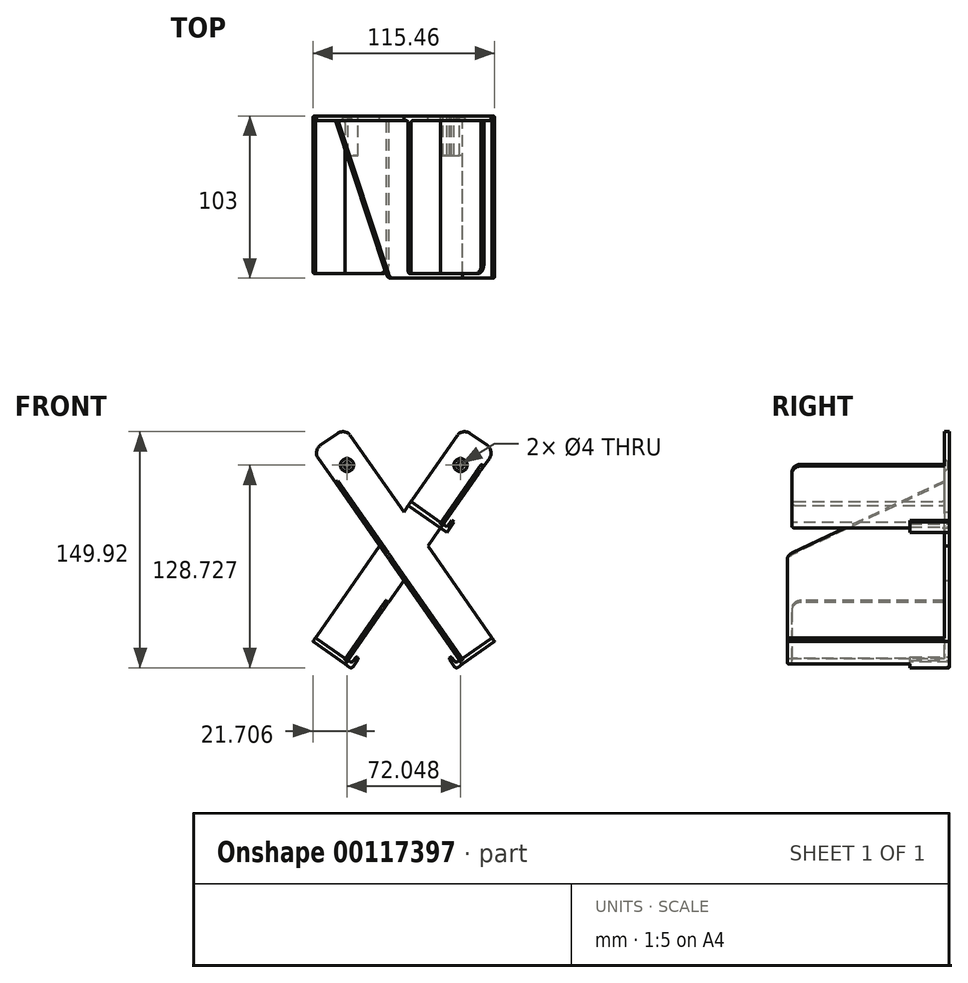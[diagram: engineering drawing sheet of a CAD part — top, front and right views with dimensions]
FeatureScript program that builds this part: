
annotation { "Feature Type Name" : "Feature", "Feature Type Description" : "" }
export const myFeature = defineFeature(function(context is Context, id is Id, definition is map)
    precondition{}
    {
        {
            var Q0;
            Q0=qCreatedBy(makeId("Front.planeOp"),FACE);
            var sketch = newSketch(context, id + "F0", { "sketchPlane" : qUnion([Q0])});
            skLineSegment(sketch, "E0", {"start": v(-100, 75) * mm, "end": v(-100, -75) * mm, "construction": true});
            skPoint(sketch, "E1", {"position": v(-100, 0) * mm});
            skLineSegment(sketch, "E2", {"start": v(57.73, 60.66) * mm, "end": v(-37.26, -75) * mm});
            skLineSegment(sketch, "E3", {"start": v(-37.26, -75) * mm, "end": v(-57.73, -60.66) * mm});
            skLineSegment(sketch, "E4", {"start": v(-57.73, -60.66) * mm, "end": v(37.26, 75) * mm});
            skLineSegment(sketch, "E5", {"start": v(37.26, 75) * mm, "end": v(57.73, 60.66) * mm});
            skLineSegment(sketch, "E6", {"start": v(47.5, 67.83) * mm, "end": v(-47.5, -67.83) * mm, "construction": true});
            skLineSegment(sketch, "E7", {"start": v(-10.24, 7.17) * mm, "end": v(10.24, -7.17) * mm, "construction": true});
            skPoint(sketch, "E8", {"position": v(0, 0) * mm});
            skLineSegment(sketch, "E9", {"start": v(-37.26, 75) * mm, "end": v(57.73, -60.66) * mm});
            skLineSegment(sketch, "E10", {"start": v(57.73, -60.66) * mm, "end": v(37.26, -75) * mm});
            skLineSegment(sketch, "E11", {"start": v(37.26, -75) * mm, "end": v(-57.73, 60.66) * mm});
            skLineSegment(sketch, "E12", {"start": v(-57.73, 60.66) * mm, "end": v(-37.26, 75) * mm});
            skLineSegment(sketch, "E13", {"start": v(-47.5, 67.83) * mm, "end": v(47.5, -67.83) * mm, "construction": true});
            skLineSegment(sketch, "E14", {"start": v(-10.24, -7.17) * mm, "end": v(10.24, 7.17) * mm, "construction": true});
            skLineSegment(sketch, "E15", {"start": v(37.26, -75) * mm, "end": v(33.16, -77.87) * mm});
            skLineSegment(sketch, "E16", {"start": v(33.16, -77.87) * mm, "end": v(28.57, -71.31) * mm});
            skLineSegment(sketch, "E17", {"start": v(28.57, -71.31) * mm, "end": v(30.2, -70.17) * mm});
            skLineSegment(sketch, "E18", {"start": v(30.2, -70.17) * mm, "end": v(33.08, -74.26) * mm});
            skLineSegment(sketch, "E19", {"start": v(33.08, -74.26) * mm, "end": v(35.54, -72.54) * mm});
            skLineSegment(sketch, "E20", {"start": v(-37.26, -75) * mm, "end": v(-33.16, -77.87) * mm});
            skLineSegment(sketch, "E21", {"start": v(-33.16, -77.87) * mm, "end": v(-28.57, -71.31) * mm});
            skLineSegment(sketch, "E22", {"start": v(-28.57, -71.31) * mm, "end": v(-30.2, -70.17) * mm});
            skLineSegment(sketch, "E23", {"start": v(-30.2, -70.17) * mm, "end": v(-33.08, -74.26) * mm});
            skLineSegment(sketch, "E24", {"start": v(-33.08, -74.26) * mm, "end": v(-35.54, -72.54) * mm});
            skLineSegment(sketch, "E25", {"start": v(23.32, 11.51) * mm, "end": v(27.42, 8.64) * mm});
            skLineSegment(sketch, "E26", {"start": v(27.42, 8.64) * mm, "end": v(32, 15.2) * mm});
            skLineSegment(sketch, "E27", {"start": v(32, 15.2) * mm, "end": v(30.37, 16.34) * mm});
            skLineSegment(sketch, "E28", {"start": v(30.37, 16.34) * mm, "end": v(27.5, 12.25) * mm});
            skLineSegment(sketch, "E29", {"start": v(27.5, 12.25) * mm, "end": v(25.04, 13.97) * mm});
            skLineSegment(sketch, "E30", {"start": v(-35.54, -72.54) * mm, "end": v(-56.01, -58.2) * mm});
            skLineSegment(sketch, "E31", {"start": v(25.04, 13.97) * mm, "end": v(4.56, 28.3) * mm});
            skLineSegment(sketch, "E32", {"start": v(23.32, 11.51) * mm, "end": v(2.84, 25.85) * mm});
            skCircle(sketch, "E33", {"center": v(36.02, 51.45) * mm, "radius": 2 * mm});
            skCircle(sketch, "E34", {"center": v(-36.02, 51.45) * mm, "radius": 2 * mm});
            skSolve(sketch);
        }
        {
            var Q0;
            {var subQ0=sQuery(id+"F0.wireOp",EDGE,"E12");Q0=makeQuery(id+"F0.imprint","IMPRINT",FACE,{"disambiguationData":[TD([[makeQuery(id+"F0.imprint","IMPRINT",EDGE,{"derivedFrom":subQ0}),-1.0]])]});}
            var Q1;
            {var subQ3=sQuery(id+"F0.wireOp",EDGE,"E2");var subQ5=sQuery(id+"F0.wireOp",EDGE,"E9");var subQ7=makeQuery(id+"F0.imprint","INTERSECT",VERTEX,{"derivedFrom":[subQ3,subQ5]});Q1=makeQuery(id+"F0.imprint","IMPRINT",FACE,{"disambiguationData":[TD([[makeQuery(id+"F0.imprint","IMPRINT",EDGE,{"disambiguationData":[TD([[subQ7,-1.0]])],"derivedFrom":subQ3}),-1.0]])]});}
            var Q2;
            {var subQ0=sQuery(id+"F0.wireOp",EDGE,"E5");Q2=makeQuery(id+"F0.imprint","IMPRINT",FACE,{"disambiguationData":[TD([[makeQuery(id+"F0.imprint","IMPRINT",EDGE,{"derivedFrom":subQ0}),-1.0]])]});}
            var Q3;
            {var subQ5=sQuery(id+"F0.wireOp",EDGE,"E32");Q3=makeQuery(id+"F0.imprint","IMPRINT",FACE,{"disambiguationData":[TD([[makeQuery(id+"F0.imprint","IMPRINT",EDGE,{"derivedFrom":subQ5}),1.0]])]});}
            var Q4;
            {var subQ2=sQuery(id+"F0.wireOp",EDGE,"E31");Q4=makeQuery(id+"F0.imprint","IMPRINT",FACE,{"disambiguationData":[TD([[makeQuery(id+"F0.imprint","IMPRINT",EDGE,{"derivedFrom":subQ2}),1.0]])]});}
            var Q5;
            {var subQ0=sQuery(id+"F0.wireOp",EDGE,"E30");Q5=makeQuery(id+"F0.imprint","IMPRINT",FACE,{"disambiguationData":[TD([[makeQuery(id+"F0.imprint","IMPRINT",EDGE,{"derivedFrom":subQ0}),-1.0]])]});}
            var Q6;
            {var subQ6=sQuery(id+"F0.wireOp",EDGE,"E10");Q6=makeQuery(id+"F0.imprint","IMPRINT",FACE,{"disambiguationData":[TD([[makeQuery(id+"F0.imprint","IMPRINT",EDGE,{"derivedFrom":subQ6}),-1.0]])]});}
            var Q7;
            {var subQ2=sQuery(id+"F0.wireOp",EDGE,"E3");Q7=makeQuery(id+"F0.imprint","IMPRINT",FACE,{"disambiguationData":[TD([[makeQuery(id+"F0.imprint","IMPRINT",EDGE,{"derivedFrom":subQ2}),-1.0]])]});}
            extrude(context, id + "F1", {"entities" : qUnion([Q0, Q1, Q2, Q3, Q4, Q5, Q6, Q7]), "depth" : 3 * mm});
        }
        {
            var Q0;
            {var subQ0=sQuery(id+"F0.wireOp",EDGE,"E11");Q0=makeQuery(id+"F1.opExtrude","SWEPT_FACE",FACE,{"disambiguationData":[OSD([subQ0]),TDD([makeQuery(id+"F0.imprint","IMPRINT",EDGE,{"disambiguationData":[TD([[makeQuery(id+"F0.imprint","INTERSECT",VERTEX,{"derivedFrom":[sQuery(id+"F0.wireOp",EDGE,"E10"),subQ0]}),-1.0]])],"derivedFrom":subQ0})])]});}
            cPlane(context, id + "F2", {"entities" : qUnion([Q0]), "cplaneType" : CPlaneType.OFFSET, "offset" : 0 * mm, "width" : 150 * mm, "height" : 150 * mm});
        }
        {
            var Q0;
            Q0=qCreatedBy(id+"F2.planeOp",FACE);
            var sketch = newSketch(context, id + "F3", { "sketchPlane" : qUnion([Q0])});
            skLineSegment(sketch, "E35.bottom", {"start": v(103, -82.8) * mm, "end": v(3, -82.8) * mm});
            skLineSegment(sketch, "E35.top", {"start": v(103, 0.2) * mm, "end": v(3, 0.2) * mm});
            skLineSegment(sketch, "E35.left", {"start": v(103, -82.8) * mm, "end": v(103, 0.2) * mm});
            skLineSegment(sketch, "E35.right", {"start": v(3, -82.8) * mm, "end": v(3, 0.2) * mm});
            skLineSegment(sketch, "E36", {"start": v(3, 0.2) * mm, "end": v(3, 57.93) * mm});
            skLineSegment(sketch, "E37", {"start": v(3, 57.93) * mm, "end": v(103, 0.2) * mm});
            skCircle(sketch, "E38.cCircle", {"center": v(48.07, -28.22) * mm, "radius": 42.07 * mm, "construction": true});
            skLineSegment(sketch, "E38.0", {"start": v(6, -3.93) * mm, "end": v(48.07, 20.36) * mm});
            skLineSegment(sketch, "E38.1", {"start": v(48.07, 20.36) * mm, "end": v(90.15, -3.93) * mm});
            skLineSegment(sketch, "E38.2", {"start": v(90.15, -3.93) * mm, "end": v(90.15, -52.51) * mm});
            skLineSegment(sketch, "E38.3", {"start": v(90.15, -52.51) * mm, "end": v(48.07, -76.8) * mm});
            skLineSegment(sketch, "E38.4", {"start": v(48.07, -76.8) * mm, "end": v(6, -52.51) * mm});
            skLineSegment(sketch, "E38.5", {"start": v(6, -52.51) * mm, "end": v(6, -3.93) * mm});
            skPoint(sketch, "E38.0.midPoint", {"position": v(27.04, 8.21) * mm});
            skLineSegment(sketch, "E39", {"start": v(103, -79.8) * mm, "end": v(3, -79.8) * mm});
            skSolve(sketch);
        }
        {
            var Q0;
            {var subQ11=sQuery(id+"F3.wireOp",EDGE,"E38.2");Q0=makeQuery(id+"F3.imprint","IMPRINT",FACE,{"disambiguationData":[TD([[makeQuery(id+"F3.imprint","IMPRINT",EDGE,{"derivedFrom":subQ11}),1.0]])]});}
            var Q1;
            {var subQ7=sQuery(id+"F3.wireOp",EDGE,"E36");Q1=makeQuery(id+"F3.imprint","IMPRINT",FACE,{"disambiguationData":[TD([[makeQuery(id+"F3.imprint","IMPRINT",EDGE,{"derivedFrom":subQ7}),-1.0]])]});}
            var Q2;
            {var subQ0=sQuery(id+"F3.wireOp",EDGE,"E38.2");Q2=makeQuery(id+"F3.imprint","IMPRINT",FACE,{"disambiguationData":[TD([[makeQuery(id+"F3.imprint","IMPRINT",EDGE,{"derivedFrom":subQ0}),-1.0]])]});}
            var Q3;
            {var subQ0=sQuery(id+"F3.wireOp",EDGE,"E38.1");var subQ1=sQuery(id+"F3.wireOp",EDGE,"E35.top");var subQ2=makeQuery(id+"F3.imprint","INTERSECT",VERTEX,{"derivedFrom":[subQ1,subQ0]});Q3=makeQuery(id+"F3.imprint","IMPRINT",FACE,{"disambiguationData":[TD([[makeQuery(id+"F3.imprint","IMPRINT",EDGE,{"disambiguationData":[TD([[subQ2,-1.0]])],"derivedFrom":subQ1}),-1.0]])]});}
            extrude(context, id + "F4", {"entities" : qUnion([Q0, Q1, Q2, Q3]), "operationType" : NewBodyOperationType.ADD, "oppositeDirection" : true, "depth" : 2 * mm});
        }
        {
            var Q0;
            {var subQ2=sQuery(id+"F3.wireOp",EDGE,"E35.bottom");Q0=makeQuery(id+"F3.imprint","IMPRINT",FACE,{"disambiguationData":[TD([[makeQuery(id+"F3.imprint","IMPRINT",EDGE,{"derivedFrom":subQ2}),-1.0]])]});}
            extrude(context, id + "F5", {"entities" : qUnion([Q0]), "operationType" : NewBodyOperationType.ADD, "oppositeDirection" : true, "depth" : 25 * mm});
        }
        {
            var Q0;
            {var subQ2=sQuery(id+"F0.wireOp",EDGE,"E20");Q0=makeQuery(id+"F0.imprint","IMPRINT",FACE,{"disambiguationData":[TD([[makeQuery(id+"F0.imprint","IMPRINT",EDGE,{"derivedFrom":subQ2}),1.0]])]});}
            var Q1;
            {var subQ2=sQuery(id+"F0.wireOp",EDGE,"E15");Q1=makeQuery(id+"F0.imprint","IMPRINT",FACE,{"disambiguationData":[TD([[makeQuery(id+"F0.imprint","IMPRINT",EDGE,{"derivedFrom":subQ2}),-1.0]])]});}
            var Q2;
            {var subQ2=sQuery(id+"F0.wireOp",EDGE,"E25");Q2=makeQuery(id+"F0.imprint","IMPRINT",FACE,{"disambiguationData":[TD([[makeQuery(id+"F0.imprint","IMPRINT",EDGE,{"derivedFrom":subQ2}),1.0]])]});}
            extrude(context, id + "F6", {"entities" : qUnion([Q0, Q1, Q2]), "operationType" : NewBodyOperationType.ADD, "depth" : 25 * mm});
        }
        {
            var Q0;
            {var subQ2=sQuery(id+"F0.wireOp",EDGE,"E3");Q0=makeQuery(id+"F0.imprint","IMPRINT",FACE,{"disambiguationData":[TD([[makeQuery(id+"F0.imprint","IMPRINT",EDGE,{"derivedFrom":subQ2}),-1.0]])]});}
            var Q1;
            {var subQ2=sQuery(id+"F0.wireOp",EDGE,"E31");Q1=makeQuery(id+"F0.imprint","IMPRINT",FACE,{"disambiguationData":[TD([[makeQuery(id+"F0.imprint","IMPRINT",EDGE,{"derivedFrom":subQ2}),1.0]])]});}
            extrude(context, id + "F7", {"entities" : qUnion([Q0, Q1]), "operationType" : NewBodyOperationType.ADD, "depth" : 100 * mm});
        }
        {
            var Q0;
            {var subQ0=sQuery(id+"F0.wireOp",EDGE,"E2");Q0=makeQuery(id+"F1.opExtrude","SWEPT_FACE",FACE,{"disambiguationData":[OSD([subQ0]),TDD([makeQuery(id+"F0.imprint","IMPRINT",EDGE,{"disambiguationData":[TD([[makeQuery(id+"F0.imprint","INTERSECT",VERTEX,{"derivedFrom":[subQ0,sQuery(id+"F0.wireOp",EDGE,"E11")]}),-1.0]])],"derivedFrom":subQ0}),makeQuery(id+"F0.imprint","IMPRINT",EDGE,{"disambiguationData":[TD([[makeQuery(id+"F0.imprint","INTERSECT",VERTEX,{"derivedFrom":[subQ0,sQuery(id+"F0.wireOp",EDGE,"E3"),sQuery(id+"F0.wireOp",EDGE,"E20")]}),1.0]])],"derivedFrom":subQ0})])]});}
            cPlane(context, id + "F8", {"entities" : qUnion([Q0]), "cplaneType" : CPlaneType.OFFSET, "offset" : 0 * mm, "width" : 150 * mm, "height" : 150 * mm});
        }
        {
            var Q0;
            Q0=qCreatedBy(id+"F8.planeOp",FACE);
            var sketch = newSketch(context, id + "F9", { "sketchPlane" : qUnion([Q0])});
            skLineSegment(sketch, "E40.bottom", {"start": v(-3, -79.8) * mm, "end": v(-100, -79.8) * mm});
            skLineSegment(sketch, "E40.top", {"start": v(-3, -34.8) * mm, "end": v(-100, -34.8) * mm});
            skLineSegment(sketch, "E40.left", {"start": v(-3, -79.8) * mm, "end": v(-3, -34.8) * mm});
            skLineSegment(sketch, "E40.right", {"start": v(-100, -79.8) * mm, "end": v(-100, -34.8) * mm});
            skLineSegment(sketch, "E41.bottom", {"start": v(-3, 70.8) * mm, "end": v(-100, 70.8) * mm});
            skLineSegment(sketch, "E41.top", {"start": v(-3, 25.8) * mm, "end": v(-100, 25.8) * mm});
            skLineSegment(sketch, "E41.left", {"start": v(-3, 70.8) * mm, "end": v(-3, 25.8) * mm});
            skLineSegment(sketch, "E41.right", {"start": v(-100, 70.8) * mm, "end": v(-100, 25.8) * mm});
            skCircle(sketch, "E42.cCircle", {"center": v(-74.95, -57.3) * mm, "radius": 16.5 * mm, "construction": true});
            skLineSegment(sketch, "E42.0", {"start": v(-84.47, -40.8) * mm, "end": v(-65.42, -40.8) * mm});
            skLineSegment(sketch, "E42.1", {"start": v(-65.42, -40.8) * mm, "end": v(-55.9, -57.3) * mm});
            skLineSegment(sketch, "E42.2", {"start": v(-55.9, -57.3) * mm, "end": v(-65.42, -73.8) * mm});
            skLineSegment(sketch, "E42.3", {"start": v(-65.42, -73.8) * mm, "end": v(-84.47, -73.8) * mm});
            skLineSegment(sketch, "E42.4", {"start": v(-84.47, -73.8) * mm, "end": v(-94, -57.3) * mm});
            skLineSegment(sketch, "E42.5", {"start": v(-94, -57.3) * mm, "end": v(-84.47, -40.8) * mm});
            skPoint(sketch, "E42.0.midPoint", {"position": v(-74.95, -40.8) * mm});
            skCircle(sketch, "E43.cCircle", {"center": v(-28.05, -57.3) * mm, "radius": 16.5 * mm, "construction": true});
            skLineSegment(sketch, "E43.0", {"start": v(-18.53, -73.8) * mm, "end": v(-37.58, -73.8) * mm});
            skLineSegment(sketch, "E43.1", {"start": v(-37.58, -73.8) * mm, "end": v(-47.1, -57.3) * mm});
            skLineSegment(sketch, "E43.2", {"start": v(-47.1, -57.3) * mm, "end": v(-37.58, -40.8) * mm});
            skLineSegment(sketch, "E43.3", {"start": v(-37.58, -40.8) * mm, "end": v(-18.53, -40.8) * mm});
            skLineSegment(sketch, "E43.4", {"start": v(-18.53, -40.8) * mm, "end": v(-9, -57.3) * mm});
            skLineSegment(sketch, "E43.5", {"start": v(-9, -57.3) * mm, "end": v(-18.53, -73.8) * mm});
            skPoint(sketch, "E43.0.midPoint", {"position": v(-28.05, -73.8) * mm});
            skCircle(sketch, "E44.cCircle", {"center": v(-74.95, 48.3) * mm, "radius": 16.5 * mm, "construction": true});
            skLineSegment(sketch, "E44.0", {"start": v(-65.42, 31.8) * mm, "end": v(-84.47, 31.8) * mm});
            skLineSegment(sketch, "E44.1", {"start": v(-84.47, 31.8) * mm, "end": v(-94, 48.3) * mm});
            skLineSegment(sketch, "E44.2", {"start": v(-94, 48.3) * mm, "end": v(-84.47, 64.8) * mm});
            skLineSegment(sketch, "E44.3", {"start": v(-84.47, 64.8) * mm, "end": v(-65.42, 64.8) * mm});
            skLineSegment(sketch, "E44.4", {"start": v(-65.42, 64.8) * mm, "end": v(-55.9, 48.3) * mm});
            skLineSegment(sketch, "E44.5", {"start": v(-55.9, 48.3) * mm, "end": v(-65.42, 31.8) * mm});
            skPoint(sketch, "E44.0.midPoint", {"position": v(-74.95, 31.8) * mm});
            skCircle(sketch, "E45.cCircle", {"center": v(-28.05, 48.3) * mm, "radius": 16.5 * mm, "construction": true});
            skLineSegment(sketch, "E45.0", {"start": v(-18.53, 31.8) * mm, "end": v(-37.58, 31.8) * mm});
            skLineSegment(sketch, "E45.1", {"start": v(-37.58, 31.8) * mm, "end": v(-47.1, 48.3) * mm});
            skLineSegment(sketch, "E45.2", {"start": v(-47.1, 48.3) * mm, "end": v(-37.58, 64.8) * mm});
            skLineSegment(sketch, "E45.3", {"start": v(-37.58, 64.8) * mm, "end": v(-18.53, 64.8) * mm});
            skLineSegment(sketch, "E45.4", {"start": v(-18.53, 64.8) * mm, "end": v(-9, 48.3) * mm});
            skLineSegment(sketch, "E45.5", {"start": v(-9, 48.3) * mm, "end": v(-18.53, 31.8) * mm});
            skPoint(sketch, "E45.0.midPoint", {"position": v(-28.05, 31.8) * mm});
            skSolve(sketch);
        }
        {
            var Q0;
            Q0=makeQuery(id+"F9.imprint","IMPRINT",FACE,{"disambiguationData":[TD([[makeQuery(id+"F9.imprint","IMPRINT",EDGE,{"derivedFrom":sQuery(id+"F9.wireOp",EDGE,"E40.bottom")}),-1.0]])]});
            var Q1;
            Q1=makeQuery(id+"F9.imprint","IMPRINT",FACE,{"disambiguationData":[TD([[makeQuery(id+"F9.imprint","IMPRINT",EDGE,{"derivedFrom":sQuery(id+"F9.wireOp",EDGE,"E41.bottom")}),1.0]])]});
            var Q2;
            Q2=makeQuery(id+"F9.imprint","IMPRINT",FACE,{"disambiguationData":[TD([[makeQuery(id+"F9.imprint","IMPRINT",EDGE,{"derivedFrom":sQuery(id+"F9.wireOp",EDGE,"E44.0")}),-1.0]])]});
            var Q3;
            Q3=makeQuery(id+"F9.imprint","IMPRINT",FACE,{"disambiguationData":[TD([[makeQuery(id+"F9.imprint","IMPRINT",EDGE,{"derivedFrom":sQuery(id+"F9.wireOp",EDGE,"E45.0")}),-1.0]])]});
            var Q4;
            Q4=makeQuery(id+"F9.imprint","IMPRINT",FACE,{"disambiguationData":[TD([[makeQuery(id+"F9.imprint","IMPRINT",EDGE,{"derivedFrom":sQuery(id+"F9.wireOp",EDGE,"E42.0")}),-1.0]])]});
            var Q5;
            Q5=makeQuery(id+"F9.imprint","IMPRINT",FACE,{"disambiguationData":[TD([[makeQuery(id+"F9.imprint","IMPRINT",EDGE,{"derivedFrom":sQuery(id+"F9.wireOp",EDGE,"E43.0")}),-1.0]])]});
            extrude(context, id + "F10", {"entities" : qUnion([Q0, Q1, Q2, Q3, Q4, Q5]), "operationType" : NewBodyOperationType.ADD, "oppositeDirection" : true, "depth" : 2 * mm});
        }
        {
            var Q0;
            Q0=makeQuery(id+"F10.opExtrude","SWEPT_EDGE",EDGE,{"disambiguationData":[OSD([sQuery(id+"F9.wireOp",EDGE,"E40.top"),sQuery(id+"F9.wireOp",EDGE,"E40.left")])]});
            var Q1;
            Q1=makeQuery(id+"F10.opExtrude","SWEPT_EDGE",EDGE,{"disambiguationData":[OSD([sQuery(id+"F9.wireOp",EDGE,"E40.top"),sQuery(id+"F9.wireOp",EDGE,"E40.right")])]});
            var Q2;
            Q2=makeQuery(id+"F10.opExtrude","SWEPT_EDGE",EDGE,{"disambiguationData":[OSD([sQuery(id+"F9.wireOp",EDGE,"E41.bottom"),sQuery(id+"F9.wireOp",EDGE,"E41.right")])]});
            var Q3;
            Q3=makeQuery(id+"F10.opExtrude","SWEPT_EDGE",EDGE,{"disambiguationData":[OSD([sQuery(id+"F9.wireOp",EDGE,"E41.bottom"),sQuery(id+"F9.wireOp",EDGE,"E41.left")])]});
            var Q4;
            Q4=makeQuery(id+"F4.opExtrude","SWEPT_EDGE",EDGE,{"disambiguationData":[OSD([sQuery(id+"F3.wireOp",EDGE,"E36"),sQuery(id+"F3.wireOp",EDGE,"E37")])]});
            var Q5;
            Q5=makeQuery(id+"F4.opExtrude","SWEPT_EDGE",EDGE,{"disambiguationData":[OSD([sQuery(id+"F3.wireOp",EDGE,"E35.top"),sQuery(id+"F3.wireOp",EDGE,"E35.left"),sQuery(id+"F3.wireOp",EDGE,"E37")])]});
            var Q6;
            Q6=makeQuery(id+"F1.opExtrude","SWEPT_EDGE",EDGE,{"disambiguationData":[OSD([sQuery(id+"F0.wireOp",EDGE,"E11"),sQuery(id+"F0.wireOp",EDGE,"E12")])]});
            var Q7;
            Q7=makeQuery(id+"F1.opExtrude","SWEPT_EDGE",EDGE,{"disambiguationData":[OSD([sQuery(id+"F0.wireOp",EDGE,"E9"),sQuery(id+"F0.wireOp",EDGE,"E12")])]});
            var Q8;
            Q8=makeQuery(id+"F1.opExtrude","SWEPT_EDGE",EDGE,{"disambiguationData":[OSD([sQuery(id+"F0.wireOp",EDGE,"E4"),sQuery(id+"F0.wireOp",EDGE,"E5")])]});
            var Q9;
            Q9=makeQuery(id+"F1.opExtrude","SWEPT_EDGE",EDGE,{"disambiguationData":[OSD([sQuery(id+"F0.wireOp",EDGE,"E2"),sQuery(id+"F0.wireOp",EDGE,"E5")])]});
            fillet(context, id + "F11", {"entities" : qUnion([Q0, Q1, Q2, Q3, Q4, Q5, Q6, Q7, Q8, Q9]), "radius" : 6 * mm, "tangentPropagation" : true, "allowEdgeOverflow" : false});
        }
        {
            var Q0;
            Q0=makeQuery(id+"F7.opExtrude","CAP_EDGE",EDGE,{"disambiguationData":[OSD([sQuery(id+"F0.wireOp",EDGE,"E3")])],"isStart":false});
            var Q1;
            Q1=makeQuery(id+"F7.opExtrude","CAP_EDGE",EDGE,{"disambiguationData":[OSD([sQuery(id+"F0.wireOp",EDGE,"E32")])],"isStart":false});
            var Q2;
            Q2=makeQuery(id+"F7.opExtrude","CAP_EDGE",EDGE,{"disambiguationData":[OSD([sQuery(id+"F0.wireOp",EDGE,"E31")])],"isStart":false});
            var Q3;
            Q3=makeQuery(id+"F5.opExtrude","SWEPT_EDGE",EDGE,{"disambiguationData":[OSD([sQuery(id+"F3.wireOp",EDGE,"E35.bottom"),sQuery(id+"F3.wireOp",EDGE,"E35.left")])]});
            var Q4;
            Q4=makeQuery(id+"F5.opExtrude","SWEPT_EDGE",EDGE,{"disambiguationData":[OSD([sQuery(id+"F3.wireOp",EDGE,"E35.left"),sQuery(id+"F3.wireOp",EDGE,"E39")])]});
            var Q5;
            Q5=makeQuery(id+"F7.opExtrude","CAP_EDGE",EDGE,{"disambiguationData":[OSD([sQuery(id+"F0.wireOp",EDGE,"E30")])],"isStart":false});
            var Q6;
            {var subQ0=sQuery(id+"F0.wireOp",EDGE,"E2");var subQ1=sQuery(id+"F0.wireOp",EDGE,"E4");var subQ2=sQuery(id+"F0.wireOp",EDGE,"E5");var subQ3=sQuery(id+"F0.wireOp",EDGE,"E9");var subQ4=sQuery(id+"F0.wireOp",EDGE,"E10");var subQ5=sQuery(id+"F0.wireOp",EDGE,"E11");var subQ6=sQuery(id+"F0.wireOp",EDGE,"E12");var subQ12=sQuery(id+"F0.wireOp",EDGE,"E31");Q6=makeQuery(id+"F7.boolean.opBoolean","INTERSECT",EDGE,{"derivedFrom":[makeQuery(id+"F4.boolean.opBoolean","SPLIT",FACE,{"disambiguationData":[TD([makeQuery(id+"F1.opExtrude","SWEPT_FACE",FACE,{"disambiguationData":[OSD([subQ2])]})])],"derivedFrom":makeQuery(id+"F1.opExtrude","CAP_FACE",FACE,{"disambiguationData":[OSD([subQ0,sQuery(id+"F0.wireOp",EDGE,"E3"),subQ1,subQ2,subQ3,subQ4,subQ5,subQ6])],"isStart":false})}),makeQuery(id+"F7.opExtrude","SWEPT_FACE",FACE,{"disambiguationData":[OSD([subQ12])]})]});}
            var Q7;
            {var subQ0=sQuery(id+"F0.wireOp",EDGE,"E2");var subQ1=sQuery(id+"F0.wireOp",EDGE,"E3");var subQ2=sQuery(id+"F0.wireOp",EDGE,"E4");var subQ3=sQuery(id+"F0.wireOp",EDGE,"E10");var subQ4=sQuery(id+"F0.wireOp",EDGE,"E11");var subQ5=sQuery(id+"F0.wireOp",EDGE,"E12");var subQ7=sQuery(id+"F0.wireOp",EDGE,"E30");Q7=makeQuery(id+"F7.boolean.opBoolean","INTERSECT",EDGE,{"derivedFrom":[makeQuery(id+"F4.boolean.opBoolean","SPLIT",FACE,{"disambiguationData":[TD([makeQuery(id+"F1.opExtrude","SWEPT_FACE",FACE,{"disambiguationData":[OSD([subQ1])]})])],"derivedFrom":makeQuery(id+"F1.opExtrude","CAP_FACE",FACE,{"disambiguationData":[OSD([subQ0,subQ1,subQ2,sQuery(id+"F0.wireOp",EDGE,"E5"),sQuery(id+"F0.wireOp",EDGE,"E9"),subQ3,subQ4,subQ5])],"isStart":false})}),makeQuery(id+"F7.opExtrude","SWEPT_FACE",FACE,{"disambiguationData":[OSD([subQ7])]})]});}
            var Q8;
            {var subQ0=sQuery(id+"F0.wireOp",EDGE,"E2");var subQ1=sQuery(id+"F0.wireOp",EDGE,"E4");var subQ2=sQuery(id+"F0.wireOp",EDGE,"E5");var subQ3=sQuery(id+"F0.wireOp",EDGE,"E9");var subQ4=sQuery(id+"F0.wireOp",EDGE,"E10");var subQ5=sQuery(id+"F0.wireOp",EDGE,"E11");var subQ6=sQuery(id+"F0.wireOp",EDGE,"E12");var subQ10=sQuery(id+"F0.wireOp",EDGE,"E32");Q8=makeQuery(id+"F7.boolean.opBoolean","INTERSECT",EDGE,{"derivedFrom":[makeQuery(id+"F4.boolean.opBoolean","SPLIT",FACE,{"disambiguationData":[TD([makeQuery(id+"F1.opExtrude","SWEPT_FACE",FACE,{"disambiguationData":[OSD([subQ2])]})])],"derivedFrom":makeQuery(id+"F1.opExtrude","CAP_FACE",FACE,{"disambiguationData":[OSD([subQ0,sQuery(id+"F0.wireOp",EDGE,"E3"),subQ1,subQ2,subQ3,subQ4,subQ5,subQ6])],"isStart":false})}),makeQuery(id+"F7.opExtrude","SWEPT_FACE",FACE,{"disambiguationData":[OSD([subQ10])]})]});}
            var Q9;
            Q9=makeQuery(id+"F6.boolean.opBoolean","MERGE",EDGE,{"derivedFrom":[makeQuery(id+"F1.opExtrude","CAP_EDGE",EDGE,{"disambiguationData":[OSD([sQuery(id+"F0.wireOp",EDGE,"E3")])],"isStart":true}),makeQuery(id+"F6.opExtrude","CAP_EDGE",EDGE,{"disambiguationData":[OSD([sQuery(id+"F0.wireOp",EDGE,"E20")])],"isStart":true})]});
            var Q10;
            Q10=makeQuery(id+"F6.boolean.opBoolean","MERGE",EDGE,{"derivedFrom":[makeQuery(id+"F1.opExtrude","CAP_EDGE",EDGE,{"disambiguationData":[OSD([sQuery(id+"F0.wireOp",EDGE,"E10")])],"isStart":true}),makeQuery(id+"F6.opExtrude","CAP_EDGE",EDGE,{"disambiguationData":[OSD([sQuery(id+"F0.wireOp",EDGE,"E15")])],"isStart":true})]});
            var Q11;
            Q11=makeQuery(id+"F5.opExtrude","SWEPT_EDGE",EDGE,{"disambiguationData":[OSD([sQuery(id+"F3.wireOp",EDGE,"E35.right"),sQuery(id+"F3.wireOp",EDGE,"E39")])]});
            var Q12;
            Q12=makeQuery(id+"F6.opExtrude","SWEPT_EDGE",EDGE,{"disambiguationData":[OSD([sQuery(id+"F0.wireOp",EDGE,"E11"),sQuery(id+"F0.wireOp",EDGE,"E19")])]});
            var Q13;
            Q13=makeQuery(id+"F6.opExtrude","SWEPT_EDGE",EDGE,{"disambiguationData":[OSD([sQuery(id+"F0.wireOp",EDGE,"E23"),sQuery(id+"F0.wireOp",EDGE,"E24")])]});
            var Q14;
            {var subQ0=sQuery(id+"F0.wireOp",EDGE,"E2");var subQ1=sQuery(id+"F0.wireOp",EDGE,"E24");var subQ2=sQuery(id+"F0.wireOp",EDGE,"E30");Q14=makeQuery(id+"F10.boolean.opBoolean","MERGE",EDGE,{"derivedFrom":[makeQuery(id+"F6.boolean.opBoolean","SPLIT",EDGE,{"disambiguationData":[TD([makeQuery(id+"F6.opExtrude","CAP_FACE",FACE,{"disambiguationData":[OSD([subQ0,sQuery(id+"F0.wireOp",EDGE,"E25"),sQuery(id+"F0.wireOp",EDGE,"E26"),sQuery(id+"F0.wireOp",EDGE,"E27"),sQuery(id+"F0.wireOp",EDGE,"E28"),sQuery(id+"F0.wireOp",EDGE,"E29")])],"isStart":true})])],"derivedFrom":makeQuery(id+"F6.opExtrude","SWEPT_EDGE",EDGE,{"disambiguationData":[OSD([subQ0,subQ1,subQ2])]})}),makeQuery(id+"F10.opExtrude","CAP_EDGE",EDGE,{"disambiguationData":[OSD([sQuery(id+"F9.wireOp",EDGE,"E40.bottom")])],"isStart":true})]});}
            var Q15;
            Q15=makeQuery(id+"F6.opExtrude","SWEPT_EDGE",EDGE,{"disambiguationData":[OSD([sQuery(id+"F0.wireOp",EDGE,"E18"),sQuery(id+"F0.wireOp",EDGE,"E19")])]});
            var Q16;
            Q16=makeQuery(id+"F6.opExtrude","SWEPT_EDGE",EDGE,{"disambiguationData":[OSD([sQuery(id+"F0.wireOp",EDGE,"E15"),sQuery(id+"F0.wireOp",EDGE,"E16")])]});
            var Q17;
            Q17=makeQuery(id+"F6.opExtrude","SWEPT_EDGE",EDGE,{"disambiguationData":[OSD([sQuery(id+"F0.wireOp",EDGE,"E20"),sQuery(id+"F0.wireOp",EDGE,"E21")])]});
            fillet(context, id + "F12", {"entities" : qUnion([Q0, Q1, Q2, Q3, Q4, Q5, Q6, Q7, Q8, Q9, Q10, Q11, Q12, Q13, Q14, Q15, Q16, Q17]), "radius" : 1.5 * mm, "allowEdgeOverflow" : false});
        }
        {
            var Q0;
            Q0=makeQuery(id+"F6.opExtrude","SWEPT_EDGE",EDGE,{"disambiguationData":[OSD([sQuery(id+"F0.wireOp",EDGE,"E21"),sQuery(id+"F0.wireOp",EDGE,"E22")])]});
            var Q1;
            Q1=makeQuery(id+"F6.opExtrude","SWEPT_EDGE",EDGE,{"disambiguationData":[OSD([sQuery(id+"F0.wireOp",EDGE,"E16"),sQuery(id+"F0.wireOp",EDGE,"E17")])]});
            var Q2;
            Q2=makeQuery(id+"F6.opExtrude","SWEPT_EDGE",EDGE,{"disambiguationData":[OSD([sQuery(id+"F0.wireOp",EDGE,"E22"),sQuery(id+"F0.wireOp",EDGE,"E23")])]});
            var Q3;
            Q3=makeQuery(id+"F6.opExtrude","SWEPT_EDGE",EDGE,{"disambiguationData":[OSD([sQuery(id+"F0.wireOp",EDGE,"E17"),sQuery(id+"F0.wireOp",EDGE,"E18")])]});
            fillet(context, id + "F13", {"entities" : qUnion([Q0, Q1, Q2, Q3]), "radius" : 1 * mm, "tangentPropagation" : true, "allowEdgeOverflow" : false});
        }
        {
            var Q0;
            Q0=makeQuery(id+"F1.opExtrude","CAP_EDGE",EDGE,{"disambiguationData":[OSD([sQuery(id+"F0.wireOp",EDGE,"E34")])],"isStart":false});
            var Q1;
            Q1=makeQuery(id+"F1.opExtrude","CAP_EDGE",EDGE,{"disambiguationData":[OSD([sQuery(id+"F0.wireOp",EDGE,"E33")])],"isStart":false});
            var Q2;
            Q2=makeQuery(id+"F1.opExtrude","CAP_EDGE",EDGE,{"disambiguationData":[OSD([sQuery(id+"F0.wireOp",EDGE,"552a12af-75ee-4a86-9e34-feb576779397")])],"isStart":false});
            chamfer(context, id + "F14", {"entities" : qUnion([Q0, Q1, Q2]), "width" : 2.2 * mm, "tangentPropagation" : true});
        }
    });
